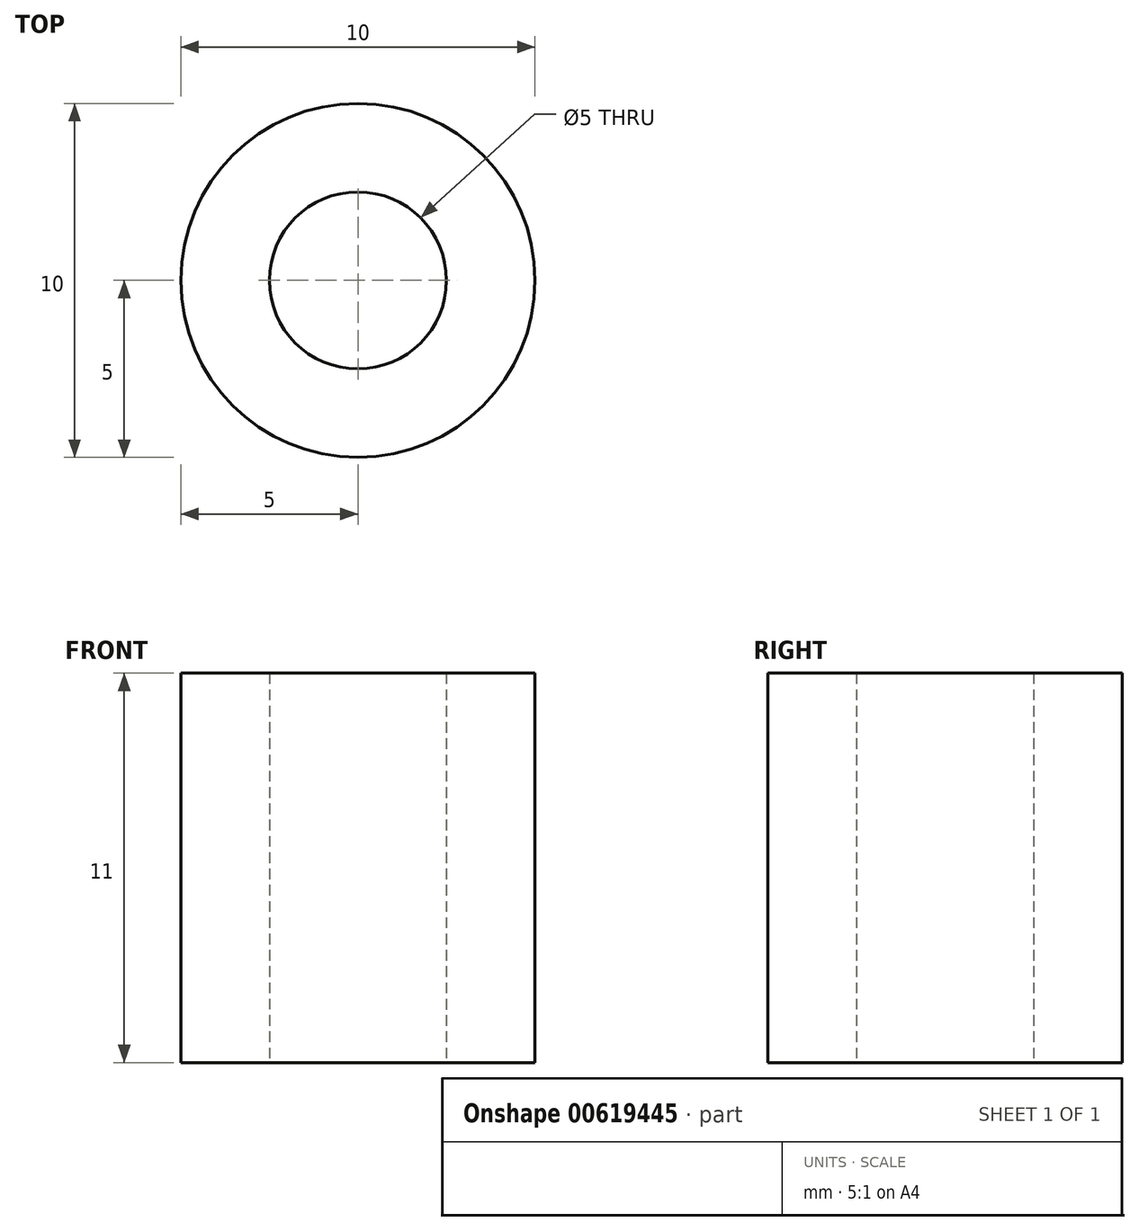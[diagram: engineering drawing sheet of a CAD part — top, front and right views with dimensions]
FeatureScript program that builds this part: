
annotation { "Feature Type Name" : "Feature", "Feature Type Description" : "" }
export const myFeature = defineFeature(function(context is Context, id is Id, definition is map)
    precondition{}
    {
        {
            var Q0;
            Q0=qCreatedBy(makeId("Top.planeOp"),FACE);
            var sketch = newSketch(context, id + "F0", { "sketchPlane" : qUnion([Q0])});
            skCircle(sketch, "E0", {"center": v(0, 0) * mm, "radius": 2.5 * mm});
            skCircle(sketch, "E1", {"center": v(0, 0) * mm, "radius": 5 * mm});
            skSolve(sketch);
        }
        {
            var Q0;
            Q0 = qSketchRegion(id + "F0", true);
            extrude(context, id + "F1", {"entities" : qUnion([Q0]), "depth" : 11 * mm, "offsetDistance" : 25 * mm});
        }
    });
